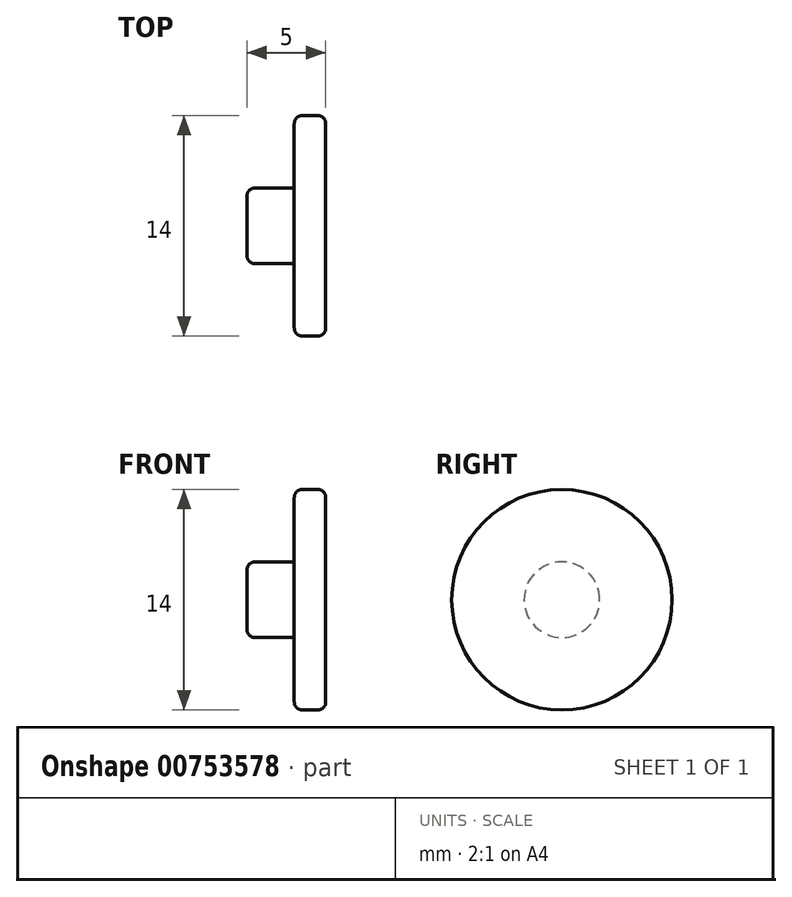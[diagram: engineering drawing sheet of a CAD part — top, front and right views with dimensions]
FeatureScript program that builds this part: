
annotation { "Feature Type Name" : "Feature", "Feature Type Description" : "" }
export const myFeature = defineFeature(function(context is Context, id is Id, definition is map)
    precondition{}
    {
        {
            var Q0;
            Q0=qCreatedBy(makeId("Right.planeOp"),FACE);
            var sketch = newSketch(context, id + "F0", { "sketchPlane" : qUnion([Q0])});
            skCircle(sketch, "E0", {"center": v(0, 0) * mm, "radius": 7 * mm});
            skCircle(sketch, "E1", {"center": v(0, 0) * mm, "radius": 2.4 * mm});
            skSolve(sketch);
        }
        {
            var Q0;
            Q0=makeQuery(id+"F0.imprint","IMPRINT",FACE,{"disambiguationData":[TD([[makeQuery(id+"F0.imprint","IMPRINT",EDGE,{"derivedFrom":sQuery(id+"F0.wireOp",EDGE,"E0")}),1.0]])]});
            var Q1;
            Q1=makeQuery(id+"F0.imprint","IMPRINT",FACE,{"disambiguationData":[TD([[makeQuery(id+"F0.imprint","IMPRINT",EDGE,{"derivedFrom":sQuery(id+"F0.wireOp",EDGE,"E1")}),1.0]])]});
            extrude(context, id + "F1", {"entities" : qUnion([Q0, Q1]), "depth" : 2 * mm, "offsetDistance" : 25.4 * mm});
        }
        {
            var Q0;
            Q0=makeQuery(id+"F0.imprint","IMPRINT",FACE,{"disambiguationData":[TD([[makeQuery(id+"F0.imprint","IMPRINT",EDGE,{"derivedFrom":sQuery(id+"F0.wireOp",EDGE,"E1")}),1.0]])]});
            extrude(context, id + "F2", {"entities" : qUnion([Q0]), "operationType" : NewBodyOperationType.ADD, "depth" : -3 * mm, "offsetDistance" : 25.4 * mm});
        }
        {
            var Q0;
            Q0=makeQuery(id+"F1.opExtrude","CAP_EDGE",EDGE,{"disambiguationData":[OSD([sQuery(id+"F0.wireOp",EDGE,"E0")])],"isStart":false});
            var Q1;
            Q1=makeQuery(id+"F2.opExtrude","CAP_EDGE",EDGE,{"disambiguationData":[OSD([sQuery(id+"F0.wireOp",EDGE,"E1")])],"isStart":false});
            var Q2;
            Q2=makeQuery(id+"F1.opExtrude","CAP_EDGE",EDGE,{"disambiguationData":[OSD([sQuery(id+"F0.wireOp",EDGE,"E0")])],"isStart":true});
            fillet(context, id + "F3", {"entities" : qUnion([Q0, Q1, Q2]), "radius" : .5 * mm, "tangentPropagation" : true, "allowEdgeOverflow" : false});
        }
    });
